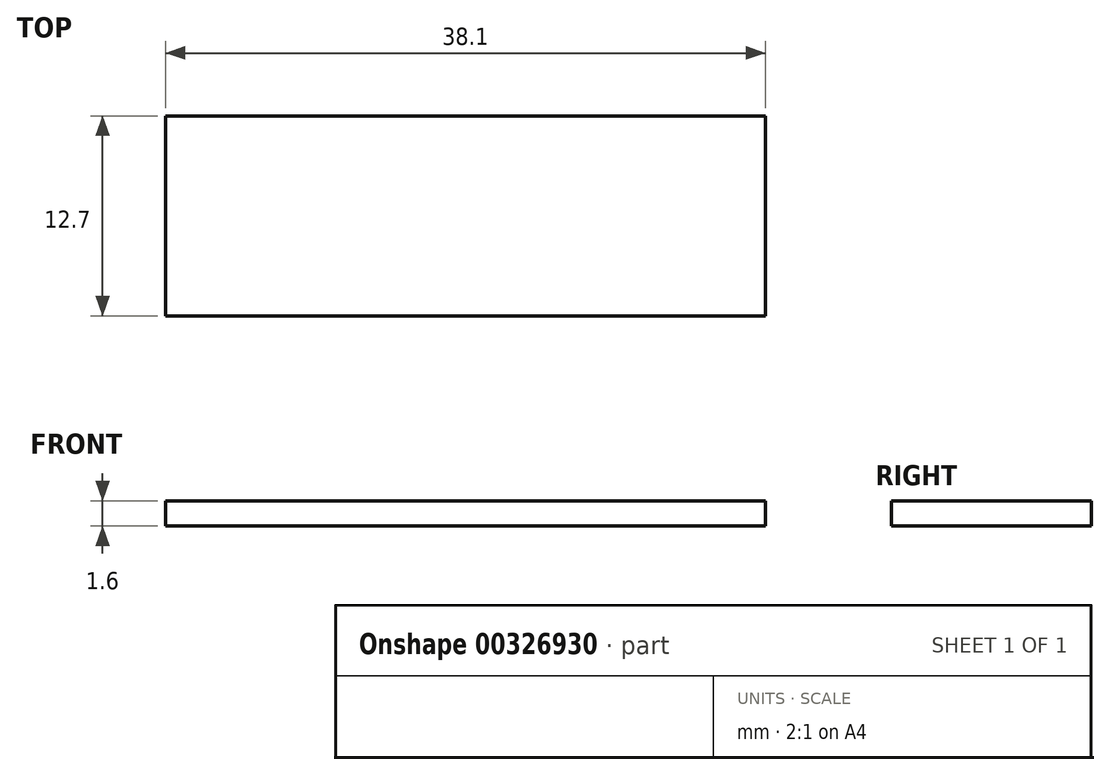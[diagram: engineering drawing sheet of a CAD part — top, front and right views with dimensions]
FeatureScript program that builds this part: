
annotation { "Feature Type Name" : "Feature", "Feature Type Description" : "" }
export const myFeature = defineFeature(function(context is Context, id is Id, definition is map)
    precondition{}
    {
        {
            var Q0;
            Q0=qCreatedBy(makeId("Top.planeOp"),FACE);
            var sketch = newSketch(context, id + "F0", { "sketchPlane" : qUnion([Q0])});
            skLineSegment(sketch, "E0.bottom", {"start": v(0, 0) * mm, "end": v(38.1, 0) * mm});
            skLineSegment(sketch, "E0.top", {"start": v(0, 12.7) * mm, "end": v(38.1, 12.7) * mm});
            skLineSegment(sketch, "E0.left", {"start": v(0, 0) * mm, "end": v(0, 12.7) * mm});
            skLineSegment(sketch, "E0.right", {"start": v(38.1, 0) * mm, "end": v(38.1, 12.7) * mm});
            skSolve(sketch);
        }
        {
            var Q0;
            Q0 = qSketchRegion(id + "F0", true);
            extrude(context, id + "F1", {"entities" : qUnion([Q0]), "depth" : 1.6 * mm});
        }
    });
